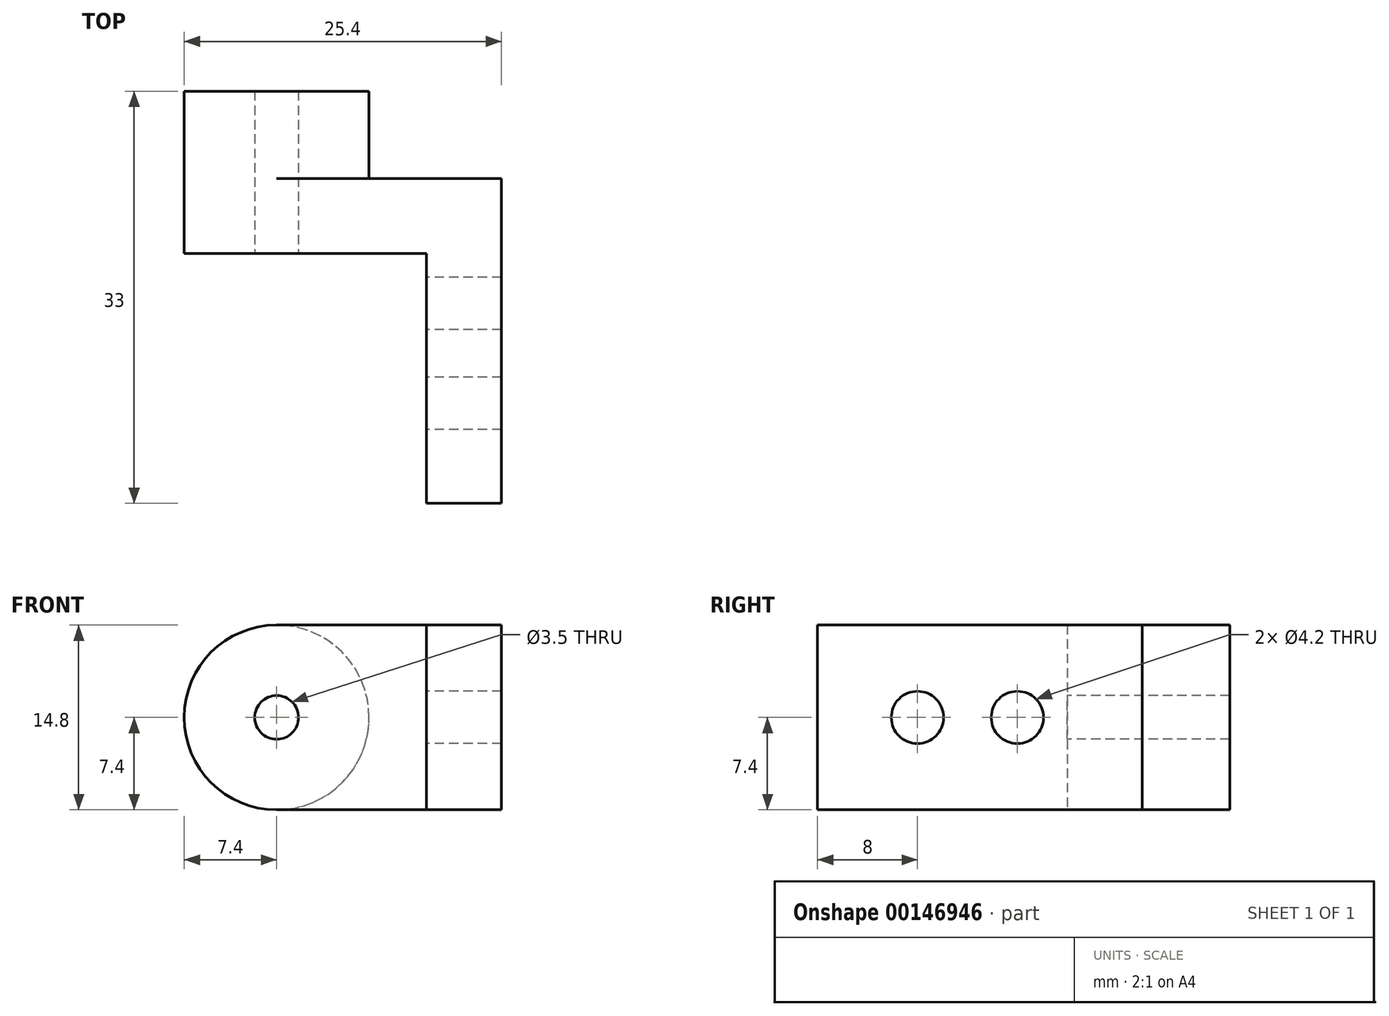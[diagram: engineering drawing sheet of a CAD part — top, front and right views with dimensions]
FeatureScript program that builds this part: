
annotation { "Feature Type Name" : "Feature", "Feature Type Description" : "" }
export const myFeature = defineFeature(function(context is Context, id is Id, definition is map)
    precondition{}
    {
        {
            var Q0;
            Q0=qCreatedBy(makeId("Front.planeOp"),FACE);
            var sketch = newSketch(context, id + "F0", { "sketchPlane" : qUnion([Q0])});
            skLineSegment(sketch, "E0", {"start": v(0, 0) * mm, "end": v(-12, 0) * mm, "construction": true});
            skCircle(sketch, "E1", {"center": v(-12, 0) * mm, "radius": 7.4 * mm});
            skLineSegment(sketch, "E2", {"start": v(-12, 7.4) * mm, "end": v(0, 7.4) * mm});
            skLineSegment(sketch, "E3", {"start": v(0, 7.4) * mm, "end": v(0, 0) * mm});
            skLineSegment(sketch, "E4.MirrorCS", {"start": v(-12, -7.4) * mm, "end": v(0, -7.4) * mm});
            skLineSegment(sketch, "E5.MirrorCS", {"start": v(0, -7.4) * mm, "end": v(0, 0) * mm});
            skLineSegment(sketch, "E6", {"start": v(0, -7.4) * mm, "end": v(6, -7.4) * mm});
            skLineSegment(sketch, "E7", {"start": v(6, -7.4) * mm, "end": v(6, 7.4) * mm});
            skLineSegment(sketch, "E8", {"start": v(0, 7.4) * mm, "end": v(6, 7.4) * mm});
            skCircle(sketch, "E9", {"center": v(-12, 0) * mm, "radius": 1.75 * mm});
            skSolve(sketch);
        }
        {
            var Q0;
            {var subQ0=sQuery(id+"F0.wireOp",EDGE,"E1");var subQ1=makeQuery(id+"F0.imprint","INTERSECT",VERTEX,{"derivedFrom":[subQ0,sQuery(id+"F0.wireOp",EDGE,"E2")]});Q0=makeQuery(id+"F0.imprint","IMPRINT",FACE,{"disambiguationData":[TD([[makeQuery(id+"F0.imprint","IMPRINT",EDGE,{"disambiguationData":[TD([[subQ1,-1.0]])],"derivedFrom":subQ0}),1.0]])]});}
            extrude(context, id + "F1", {"entities" : qUnion([Q0]), "oppositeDirection" : true, "depth" : 13 * mm});
        }
        {
            var Q0;
            {var subQ1=sQuery(id+"F0.wireOp",EDGE,"E2");Q0=makeQuery(id+"F0.imprint","IMPRINT",FACE,{"disambiguationData":[TD([[makeQuery(id+"F0.imprint","IMPRINT",EDGE,{"derivedFrom":subQ1}),-1.0]])]});}
            var Q1;
            Q1=makeQuery(id+"F0.imprint","IMPRINT",FACE,{"disambiguationData":[TD([[makeQuery(id+"F0.imprint","IMPRINT",EDGE,{"derivedFrom":sQuery(id+"F0.wireOp",EDGE,"E3")}),1.0]])]});
            extrude(context, id + "F2", {"entities" : qUnion([Q0, Q1]), "operationType" : NewBodyOperationType.ADD, "oppositeDirection" : true, "depth" : 6 * mm});
        }
        {
            var Q0;
            Q0=makeQuery(id+"F0.imprint","IMPRINT",FACE,{"disambiguationData":[TD([[makeQuery(id+"F0.imprint","IMPRINT",EDGE,{"derivedFrom":sQuery(id+"F0.wireOp",EDGE,"E3")}),1.0]])]});
            extrude(context, id + "F3", {"entities" : qUnion([Q0]), "operationType" : NewBodyOperationType.ADD, "depth" : 20 * mm});
        }
        {
            var Q0;
            Q0=qCreatedBy(makeId("Right.planeOp"),FACE);
            var sketch = newSketch(context, id + "F4", { "sketchPlane" : qUnion([Q0])});
            skLineSegment(sketch, "E10", {"start": v(-20, 0) * mm, "end": v(-12, 0) * mm, "construction": true});
            skPoint(sketch, "E11.middle", {"position": v(-12, 0) * mm});
            skLineSegment(sketch, "E12", {"start": v(-12, 0) * mm, "end": v(-4, 0) * mm, "construction": true});
            skCircle(sketch, "E13", {"center": v(-12, 0) * mm, "radius": 2.1 * mm});
            skCircle(sketch, "E14", {"center": v(-4, 0) * mm, "radius": 2.1 * mm});
            skSolve(sketch);
        }
        {
            var Q0;
            Q0 = qSketchRegion(id + "F4", true);
            extrude(context, id + "F5", {"entities" : qUnion([Q0]), "operationType" : NewBodyOperationType.REMOVE, "depth" : 25 * mm});
        }
    });
